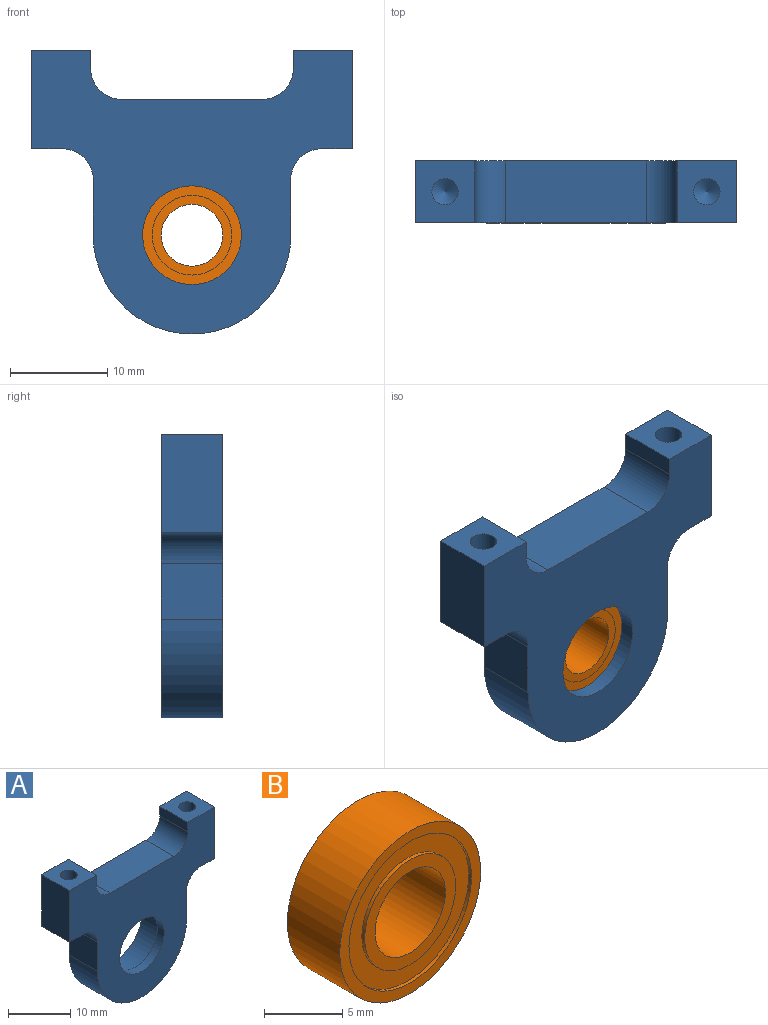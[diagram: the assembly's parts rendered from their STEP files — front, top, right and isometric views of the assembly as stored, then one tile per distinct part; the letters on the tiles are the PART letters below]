
ASSEMBLY  parts=2 mates=1
PART A: 25 faces, bbox 33x6.4x29.2 mm
  f0: cylinder r=5.08mm len=10.16mm, axis (0,1,0), area 50.3mm2, adj f19,f24
  f1: cylinder r=6.35mm len=12.7mm, axis (0,1,0), area 190.5mm2, adj f18,f24
  f2: cylinder r=1.35mm len=7.62mm, axis (0,0,1), area 64.8mm2, adj f3,f10
  f3: cone r=1.35mm half-angle=59deg, axis (0,0,1), area 6.7mm2, adj f2
  f4: cylinder r=1.35mm len=7.62mm, axis (0,0,1), area 64.8mm2, adj f5,f14
  f5: cone r=1.35mm half-angle=59deg, axis (0,0,1), area 6.7mm2, adj f4
  f6: cylinder r=10.16mm len=20.32mm, axis (0,-1,0), area 202.7mm2, adj f7,f17,f18,f19
  f7: plane 6.35x5.72mm, normal (-1,0,0), area 36.3mm2, adj f6,f18,f19,f20
  f8: plane 6.35x3.18mm, normal (0,0,-1), area 20.2mm2, adj f9,f18,f19,f20
  f9: plane 10.16x6.35mm, normal (-1,0,0), area 64.5mm2, adj f8,f10,f18,f19
  f10: plane 6.35x6.08mm, normal (0,0,1), area 32.9mm2, adj f2,f9,f11,f18,f19
  f11: plane 6.35x1.91mm, normal (1,0,0), area 12.1mm2, adj f10,f18,f19,f23
  f12: plane 14.51x6.35mm, normal (0,0,1), area 92.1mm2, adj f18,f19,f22,f23
  f13: plane 6.35x1.91mm, normal (-1,0,0), area 12.1mm2, adj f14,f18,f19,f22
  f14: plane 6.35x6.08mm, normal (0,0,1), area 32.9mm2, adj f4,f13,f15,f18,f19
  f15: plane 10.16x6.35mm, normal (1,0,0), area 64.5mm2, adj f14,f16,f18,f19
  f16: plane 6.35x3.18mm, normal (0,0,-1), area 20.2mm2, adj f15,f18,f19,f21
  f17: plane 6.35x5.72mm, normal (1,0,0), area 36.3mm2, adj f6,f18,f19,f21
  f18: plane 33.02x29.21mm, normal (0,1,0), area 454.3mm2, adj f1,f6,f7,f8,f9,f10,f11,f12
  f19: plane 33.02x29.21mm, normal (0,-1,0), area 499.9mm2, adj f0,f6,f7,f8,f9,f10,f11,f12
  f20: cylinder r=3.17mm len=6.35mm, axis (0,1,0), area 31.7mm2, adj f7,f8,f18,f19
  f21: cylinder r=3.17mm len=6.35mm, axis (0,1,0), area 31.7mm2, adj f16,f17,f18,f19
  f22: cylinder r=3.17mm len=6.35mm, axis (0,1,0), area 31.7mm2, adj f12,f13,f18,f19
  f23: cylinder r=3.17mm len=6.35mm, axis (0,1,0), area 31.7mm2, adj f11,f12,f18,f19
  f24: plane 12.7x12.7mm, normal (0,1,0), area 45.6mm2, adj f0,f1
PART B: 12 faces, bbox 12.7x4.7x12.7 mm
  f0: cylinder r=4.1mm len=8.2mm, axis (0,-1,0), area 6.5mm2, adj f6,f11
  f1: cylinder r=5.52mm len=11.05mm, axis (0,-1,0), area 8.8mm2, adj f9,f11
  f2: cylinder r=4.1mm len=8.2mm, axis (0,1,0), area 6.5mm2, adj f7,f10
  f3: cylinder r=5.52mm len=11.05mm, axis (0,1,0), area 8.8mm2, adj f8,f10
  f4: cylinder r=3.17mm len=6.35mm, axis (0,-1,0), area 94.2mm2, adj f6,f7
  f5: cylinder r=6.35mm len=12.7mm, axis (0,-1,0), area 188.5mm2, adj f8,f9
  f6: plane 8.2x8.2mm, normal (0,-1,0), area 21.2mm2, adj f0,f4
  f7: plane 8.2x8.2mm, normal (0,1,0), area 21.2mm2, adj f2,f4
  f8: plane 12.7x12.7mm, normal (0,1,0), area 30.8mm2, adj f3,f5
  f9: plane 12.7x12.7mm, normal (0,-1,0), area 30.8mm2, adj f1,f5
  f10: plane 11.05x11.05mm, normal (0,1,0), area 43mm2, adj f2,f3
  f11: plane 11.05x11.05mm, normal (0,-1,0), area 43mm2, adj f0,f1
PLACE A t=(8.38,13.25,23.53)mm
PLACE B rot(axis=(0,1,0),0deg) t=(8.38,14.83,23.53)mm
MATE fastened B.f0 <-> A.f0  axis (0,1,0) through (8.38,14.83,23.53)mm
